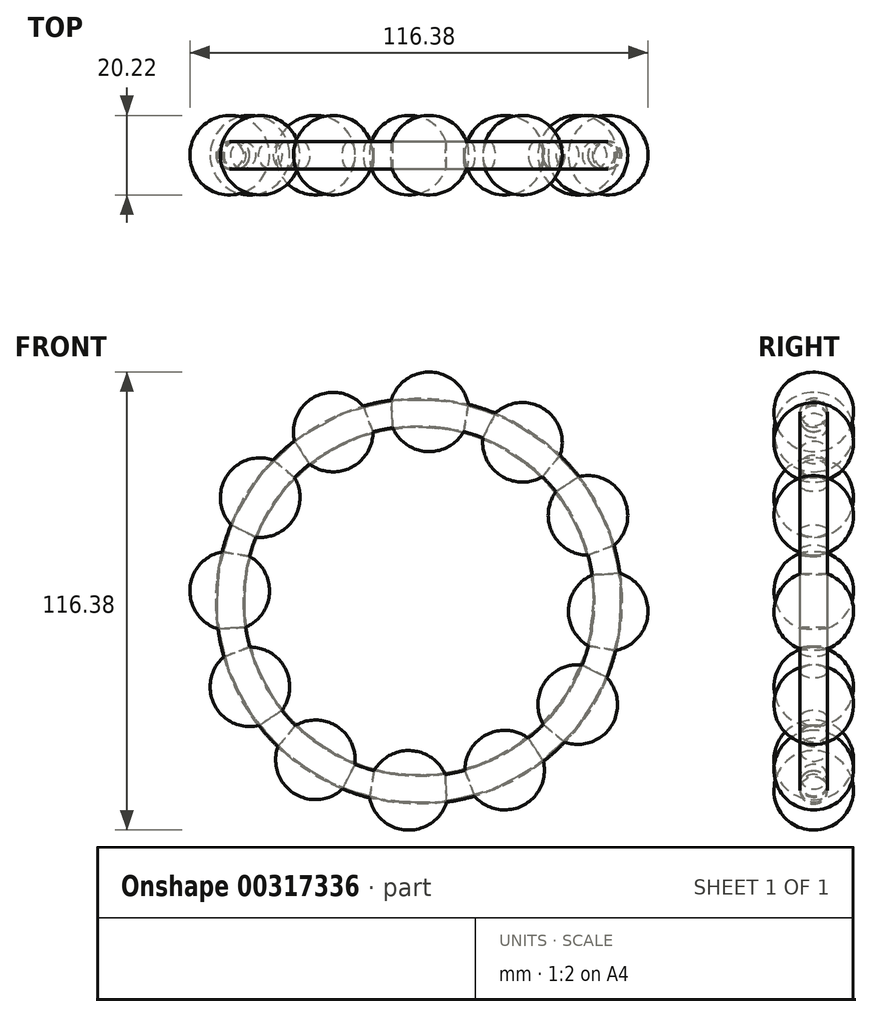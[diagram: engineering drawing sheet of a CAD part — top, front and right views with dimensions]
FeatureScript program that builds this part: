
annotation { "Feature Type Name" : "Feature", "Feature Type Description" : "" }
export const myFeature = defineFeature(function(context is Context, id is Id, definition is map)
    precondition{}
    {
        {
            var Q0;
            Q0=qCreatedBy(makeId("Right.planeOp"),FACE);
            var sketch = newSketch(context, id + "F0", { "sketchPlane" : qUnion([Q0])});
            skCircle(sketch, "E0", {"center": v(0, 48.05) * mm, "radius": 3.5 * mm});
            skLineSegment(sketch, "E1", {"start": v(14.07, 0) * mm, "end": v(-14.83, 0) * mm});
            skSolve(sketch);
        }
        {
            var Q0;
            Q0=makeQuery(id+"F0.imprint","IMPRINT",FACE,{"disambiguationData":[TD([[makeQuery(id+"F0.imprint","IMPRINT",EDGE,{"derivedFrom":sQuery(id+"F0.wireOp",EDGE,"E0")}),1.0]])]});
            var Q1;
            Q1=sQuery(id+"F0.wireOp",EDGE,"E1");
            revolve(context, id + "F1", {"entities" : qUnion([Q0]), "axis" : qUnion([Q1]), "revolveType" : RevolveType.FULL});
        }
        {
            var Q0;
            Q0=qCreatedBy(makeId("Front.planeOp"),FACE);
            var sketch = newSketch(context, id + "F2", { "sketchPlane" : qUnion([Q0])});
            skArc(sketch, "E2", {"start": v(-21.78, 32.84) * mm, "mid": v(-11.68, 42.94) * mm, "end": v(-21.78, 53.05) * mm});
            skCircle(sketch, "E3", {"center": v(0, 0) * mm, "radius": 4.88 * mm});
            skLineSegment(sketch, "E4", {"start": v(-21.78, 53.05) * mm, "end": v(-21.78, 32.84) * mm});
            skSolve(sketch);
        }
        {
            var Q0;
            Q0=makeQuery(id+"F2.imprint","IMPRINT",FACE,{"disambiguationData":[TD([[makeQuery(id+"F2.imprint","IMPRINT",EDGE,{"derivedFrom":sQuery(id+"F2.wireOp",EDGE,"E2")}),1.0]])]});
            var Q1;
            Q1=sQuery(id+"F2.wireOp",EDGE,"E4");
            revolve(context, id + "F3", {"operationType" : NewBodyOperationType.ADD, "entities" : qUnion([Q0]), "axis" : qUnion([Q1]), "revolveType" : RevolveType.FULL});
        }
        {
            var Q0;
            Q0=makeQuery(id+"F1.opRevolve","SWEPT_BODY",BODY,{"disambiguationData":[OSD([sQuery(id+"F0.wireOp",EDGE,"E0")])]});
            var Q1;
            Q1=sQuery(id+"F2.wireOp",EDGE,"E3");
            circularPattern(context, id + "F4", {"entities" : qUnion([Q0]), "axis" : qUnion([Q1]), "angle" : 360 * degree, "instanceCount" : 12, "equalSpace" : true});
        }
    });
